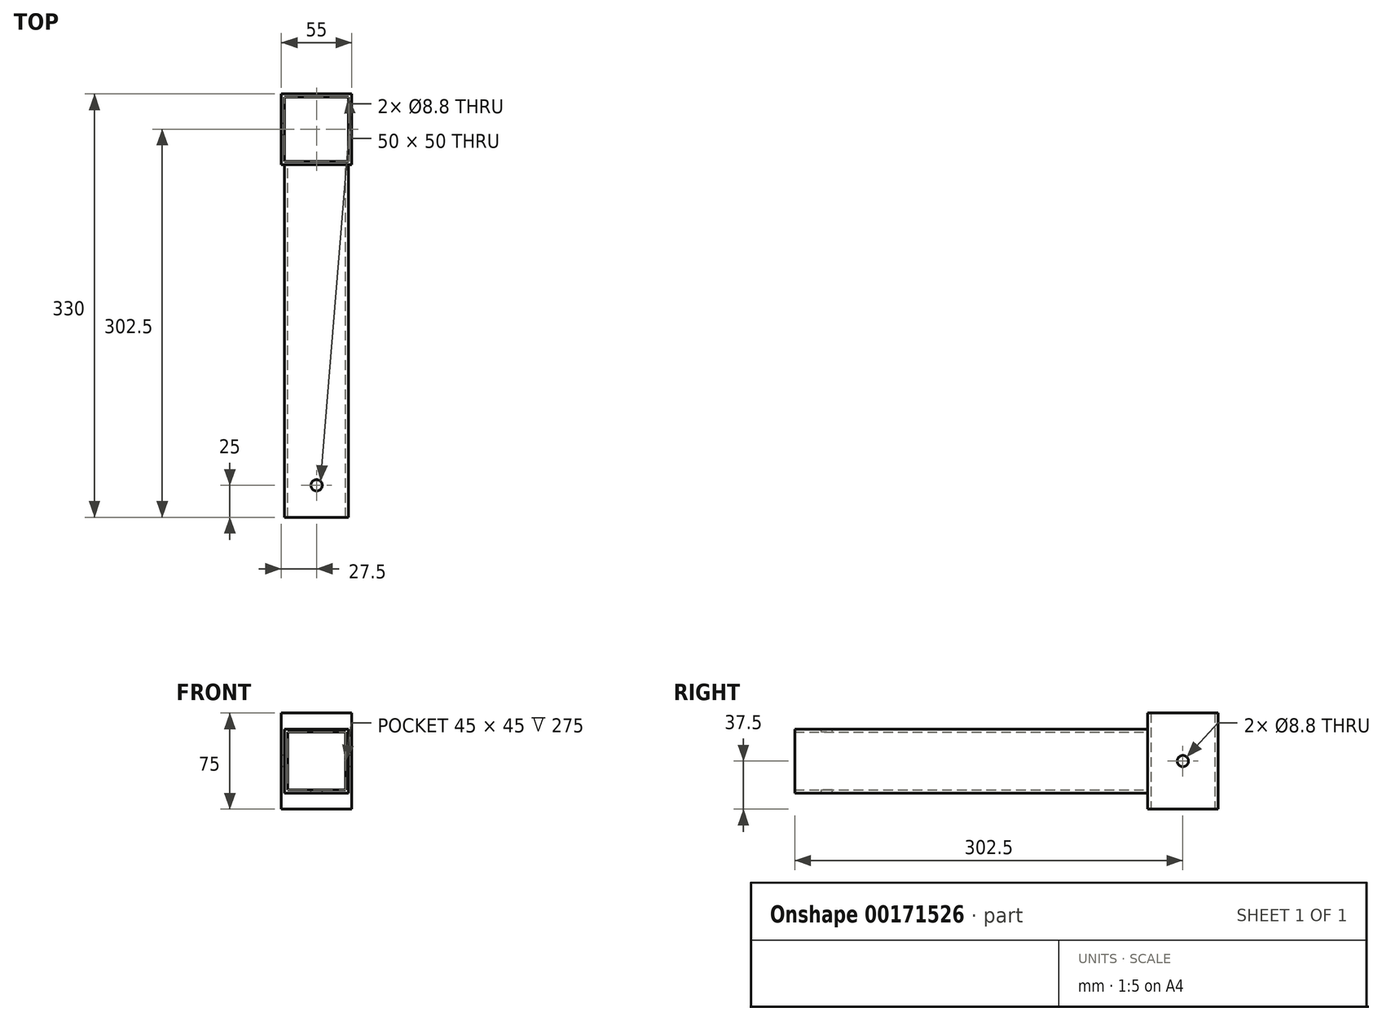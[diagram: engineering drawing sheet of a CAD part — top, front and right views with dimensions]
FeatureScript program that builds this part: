
annotation { "Feature Type Name" : "Feature", "Feature Type Description" : "" }
export const myFeature = defineFeature(function(context is Context, id is Id, definition is map)
    precondition{}
    {
        {
            var Q0;
            Q0=qCreatedBy(makeId("Top.planeOp"),FACE);
            var sketch = newSketch(context, id + "F0", { "sketchPlane" : qUnion([Q0])});
            skLineSegment(sketch, "E0.bottom", {"start": v(27.5, -27.5) * mm, "end": v(-27.5, -27.5) * mm});
            skLineSegment(sketch, "E0.top", {"start": v(27.5, 27.5) * mm, "end": v(-27.5, 27.5) * mm});
            skLineSegment(sketch, "E0.left", {"start": v(27.5, -27.5) * mm, "end": v(27.5, 27.5) * mm});
            skLineSegment(sketch, "E0.right", {"start": v(-27.5, -27.5) * mm, "end": v(-27.5, 27.5) * mm});
            skPoint(sketch, "E0.middle", {"position": v(0, 0) * mm});
            skLineSegment(sketch, "E1.bottom", {"start": v(25, -25) * mm, "end": v(-25, -25) * mm});
            skLineSegment(sketch, "E1.top", {"start": v(25, 25) * mm, "end": v(-25, 25) * mm});
            skLineSegment(sketch, "E1.left", {"start": v(25, -25) * mm, "end": v(25, 25) * mm});
            skLineSegment(sketch, "E1.right", {"start": v(-25, -25) * mm, "end": v(-25, 25) * mm});
            skSolve(sketch);
        }
        {
            var Q0;
            Q0=makeQuery(id+"F0.imprint","IMPRINT",FACE,{"disambiguationData":[TD([[makeQuery(id+"F0.imprint","IMPRINT",EDGE,{"derivedFrom":sQuery(id+"F0.wireOp",EDGE,"E0.bottom")}),-1.0]])]});
            extrude(context, id + "F1", {"entities" : qUnion([Q0]), "depth" : 75 * mm});
        }
        {
            var Q0;
            Q0=makeQuery(id+"F1.opExtrude","SWEPT_FACE",FACE,{"disambiguationData":[OSD([sQuery(id+"F0.wireOp",EDGE,"E0.right")])]});
            var sketch = newSketch(context, id + "F2", { "sketchPlane" : qUnion([Q0])});
            skPoint(sketch, "E2", {"position": v(0, 37.5) * mm});
            skPoint(sketch, "E2.positionSnap0", {"position": v(0, 75) * mm});
            skSolve(sketch);
        }
        {
            var Q0;
            Q0=sQuery(id+"F2.wireOp",VERTEX,"E2");
            var Q1;
            Q1=makeQuery(id+"F1.opExtrude","SWEPT_BODY",BODY,{"disambiguationData":[OSD([sQuery(id+"F0.wireOp",EDGE,"E0.bottom"),sQuery(id+"F0.wireOp",EDGE,"E0.top"),sQuery(id+"F0.wireOp",EDGE,"E0.left"),sQuery(id+"F0.wireOp",EDGE,"E0.right"),sQuery(id+"F0.wireOp",EDGE,"E1.bottom"),sQuery(id+"F0.wireOp",EDGE,"E1.top"),sQuery(id+"F0.wireOp",EDGE,"E1.left"),sQuery(id+"F0.wireOp",EDGE,"E1.right")])]});
            hole(context, id + "F3", {"style" : HoleStyle.SIMPLE, "endStyle" : HoleEndStyle.THROUGH, "standardTappedOrClearance" : lookupTablePath({ "standard" : "ISO", "fit" : "Normal", "size" : "M8", "type" : "Clearance" }), "standardBlindInLast" : lookupTablePath({ "fit" : "Standard", "standard" : "ISO", "size" : "M8", "type" : "Clearance" }), "holeDiameter" : 8.8 * mm, "locations" : qUnion([Q0]), "scope" : qUnion([Q1]), "isTappedThrough" : true});
        }
        {
            var Q0;
            Q0=makeQuery(id+"F1.opExtrude","SWEPT_FACE",FACE,{"disambiguationData":[OSD([sQuery(id+"F0.wireOp",EDGE,"E0.bottom")])]});
            var sketch = newSketch(context, id + "F4", { "sketchPlane" : qUnion([Q0])});
            skLineSegment(sketch, "E3.bottom", {"start": v(25, 62.5) * mm, "end": v(-25, 62.5) * mm});
            skLineSegment(sketch, "E3.top", {"start": v(25, 12.5) * mm, "end": v(-25, 12.5) * mm});
            skLineSegment(sketch, "E3.left", {"start": v(25, 62.5) * mm, "end": v(25, 12.5) * mm});
            skLineSegment(sketch, "E3.right", {"start": v(-25, 62.5) * mm, "end": v(-25, 12.5) * mm});
            skPoint(sketch, "E3.middle", {"position": v(0, 37.5) * mm});
            skPoint(sketch, "E3.middle.positionSnap0", {"position": v(-27.5, 37.5) * mm});
            skPoint(sketch, "E3.centerSnap0", {"position": v(-27.5, 37.5) * mm});
            skLineSegment(sketch, "E4.bottom", {"start": v(22.5, 15) * mm, "end": v(-22.5, 15) * mm});
            skLineSegment(sketch, "E4.top", {"start": v(22.5, 60) * mm, "end": v(-22.5, 60) * mm});
            skLineSegment(sketch, "E4.left", {"start": v(22.5, 15) * mm, "end": v(22.5, 60) * mm});
            skLineSegment(sketch, "E4.right", {"start": v(-22.5, 15) * mm, "end": v(-22.5, 60) * mm});
            skSolve(sketch);
        }
        {
            var Q0;
            Q0=makeQuery(id+"F4.imprint","IMPRINT",FACE,{"disambiguationData":[TD([[makeQuery(id+"F4.imprint","IMPRINT",EDGE,{"derivedFrom":sQuery(id+"F4.wireOp",EDGE,"E3.bottom")}),1.0]])]});
            extrude(context, id + "F5", {"entities" : qUnion([Q0]), "operationType" : NewBodyOperationType.ADD, "depth" : 275 * mm});
        }
        {
            var Q0;
            Q0=makeQuery(id+"F5.opExtrude","SWEPT_FACE",FACE,{"disambiguationData":[OSD([sQuery(id+"F4.wireOp",EDGE,"E3.bottom")])]});
            var sketch = newSketch(context, id + "F6", { "sketchPlane" : qUnion([Q0])});
            skPoint(sketch, "E5", {"position": v(0, -277.5) * mm});
            skPoint(sketch, "E5.positionSnap0", {"position": v(0, -302.5) * mm});
            skSolve(sketch);
        }
        {
            var Q0;
            Q0=sQuery(id+"F6.wireOp",VERTEX,"E5");
            var Q1;
            Q1=makeQuery(id+"F1.opExtrude","SWEPT_BODY",BODY,{"disambiguationData":[OSD([sQuery(id+"F0.wireOp",EDGE,"E0.bottom"),sQuery(id+"F0.wireOp",EDGE,"E0.top"),sQuery(id+"F0.wireOp",EDGE,"E0.left"),sQuery(id+"F0.wireOp",EDGE,"E0.right"),sQuery(id+"F0.wireOp",EDGE,"E1.bottom"),sQuery(id+"F0.wireOp",EDGE,"E1.top"),sQuery(id+"F0.wireOp",EDGE,"E1.left"),sQuery(id+"F0.wireOp",EDGE,"E1.right")])]});
            hole(context, id + "F7", {"style" : HoleStyle.SIMPLE, "endStyle" : HoleEndStyle.THROUGH, "standardTappedOrClearance" : lookupTablePath({ "standard" : "ISO", "fit" : "Normal", "size" : "M8", "type" : "Clearance" }), "standardBlindInLast" : lookupTablePath({ "fit" : "Standard", "standard" : "ISO", "size" : "M8", "type" : "Clearance" }), "holeDiameter" : 8.8 * mm, "locations" : qUnion([Q0]), "scope" : qUnion([Q1]), "isTappedThrough" : true});
        }
    });
